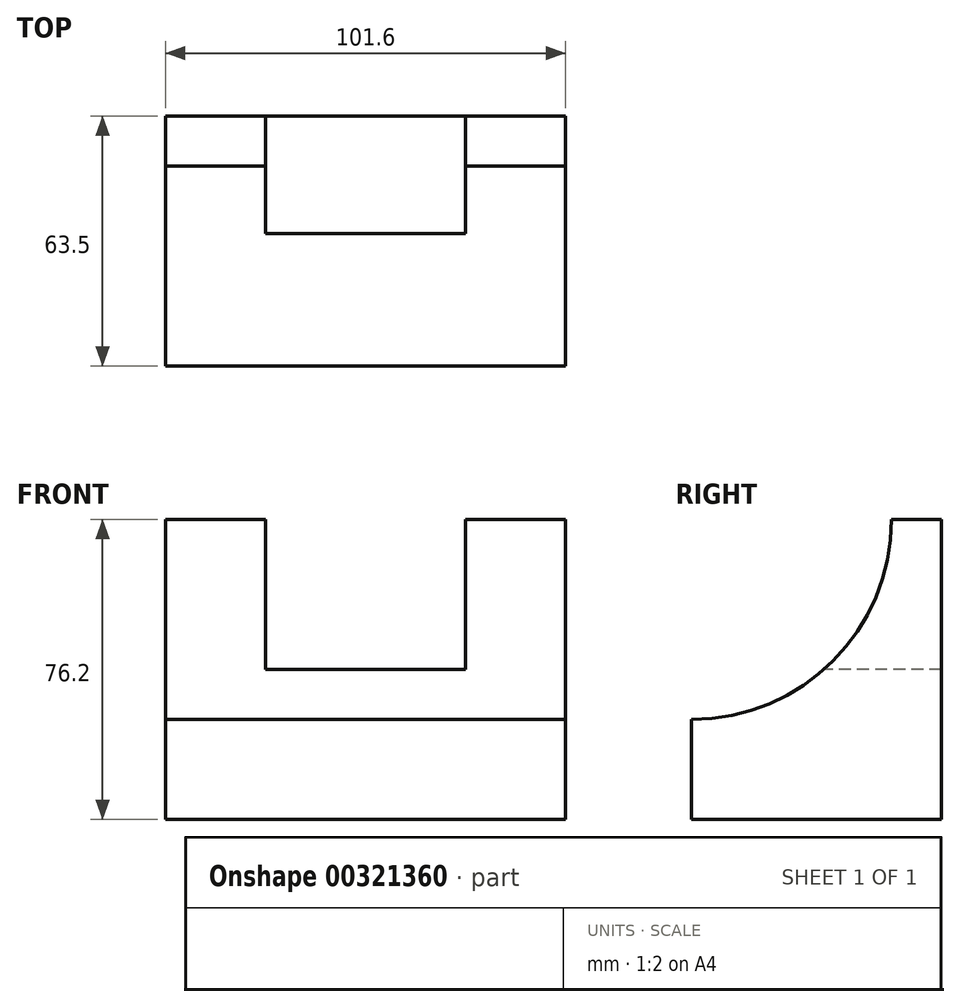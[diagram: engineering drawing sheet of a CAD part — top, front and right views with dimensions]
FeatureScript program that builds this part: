
annotation { "Feature Type Name" : "Feature", "Feature Type Description" : "" }
export const myFeature = defineFeature(function(context is Context, id is Id, definition is map)
    precondition{}
    {
        {
            var Q0;
            Q0=qCreatedBy(makeId("Front.planeOp"),FACE);
            var sketch = newSketch(context, id + "F0", { "sketchPlane" : qUnion([Q0])});
            skLineSegment(sketch, "E0.bottom", {"start": v(-49.6, 27.46) * mm, "end": v(52, 27.46) * mm});
            skLineSegment(sketch, "E0.top", {"start": v(-49.6, -48.74) * mm, "end": v(52, -48.74) * mm});
            skLineSegment(sketch, "E0.left", {"start": v(-49.6, 27.46) * mm, "end": v(-49.6, -48.74) * mm});
            skLineSegment(sketch, "E0.right", {"start": v(52, 27.46) * mm, "end": v(52, -48.74) * mm});
            skSolve(sketch);
        }
        {
            var Q0;
            Q0=makeQuery(id+"F0.imprint","IMPRINT",FACE,{"disambiguationData":[TD([[makeQuery(id+"F0.imprint","IMPRINT",EDGE,{"derivedFrom":sQuery(id+"F0.wireOp",EDGE,"E0.bottom")}),-1.0]])]});
            extrude(context, id + "F1", {"entities" : qUnion([Q0]), "depth" : 63.5 * mm});
        }
        {
            var Q0;
            Q0=makeQuery(id+"F1.opExtrude","SWEPT_FACE",FACE,{"disambiguationData":[OSD([sQuery(id+"F0.wireOp",EDGE,"E0.bottom")])]});
            var sketch = newSketch(context, id + "F2", { "sketchPlane" : qUnion([Q0])});
            skLineSegment(sketch, "E1.bottom", {"start": v(-24.2, 0) * mm, "end": v(26.6, 0) * mm});
            skLineSegment(sketch, "E1.top", {"start": v(-24.2, -12.7) * mm, "end": v(26.6, -12.7) * mm});
            skLineSegment(sketch, "E1.left", {"start": v(-24.2, 0) * mm, "end": v(-24.2, -12.7) * mm});
            skLineSegment(sketch, "E1.right", {"start": v(26.6, 0) * mm, "end": v(26.6, -12.7) * mm});
            skSolve(sketch);
        }
        {
            var Q0;
            Q0=makeQuery(id+"F2.imprint","IMPRINT",FACE,{"disambiguationData":[TD([[makeQuery(id+"F2.imprint","IMPRINT",EDGE,{"derivedFrom":sQuery(id+"F2.wireOp",EDGE,"E1.bottom")}),-1.0]])]});
            extrude(context, id + "F3", {"entities" : qUnion([Q0]), "operationType" : NewBodyOperationType.REMOVE, "oppositeDirection" : true, "depth" : 38.1 * mm});
        }
        {
            var Q0;
            Q0=makeQuery(id+"F1.opExtrude","SWEPT_FACE",FACE,{"disambiguationData":[OSD([sQuery(id+"F0.wireOp",EDGE,"E0.left")])]});
            var sketch = newSketch(context, id + "F4", { "sketchPlane" : qUnion([Q0])});
            skArc(sketch, "E2", {"start": v(12.7, 27.46) * mm, "mid": v(27.58, -8.46) * mm, "end": v(63.5, -23.34) * mm});
            skLineSegment(sketch, "E3", {"start": v(12.7, 27.46) * mm, "end": v(63.5, 27.46) * mm});
            skLineSegment(sketch, "E4", {"start": v(63.5, 27.46) * mm, "end": v(63.5, -23.34) * mm});
            skSolve(sketch);
        }
        {
            var Q0;
            Q0=makeQuery(id+"F4.imprint","IMPRINT",FACE,{"disambiguationData":[TD([[makeQuery(id+"F4.imprint","IMPRINT",EDGE,{"derivedFrom":sQuery(id+"F4.wireOp",EDGE,"E2")}),1.0]])]});
            extrude(context, id + "F5", {"entities" : qUnion([Q0]), "operationType" : NewBodyOperationType.REMOVE, "endBound" : BoundingType.THROUGH_ALL, "oppositeDirection" : true, "depth" : 25.4 * mm});
        }
        {
            var Q0;
            Q0=makeQuery(id+"F3.boolean.opBoolean","COPY",FACE,{"derivedFrom":makeQuery(id+"F3.opExtrude","SWEPT_FACE",FACE,{"disambiguationData":[OSD([sQuery(id+"F2.wireOp",EDGE,"E1.top")])]})});
            extrude(context, id + "F6", {"entities" : qUnion([Q0]), "operationType" : NewBodyOperationType.REMOVE, "oppositeDirection" : true, "depth" : 25.4 * mm});
        }
    });
